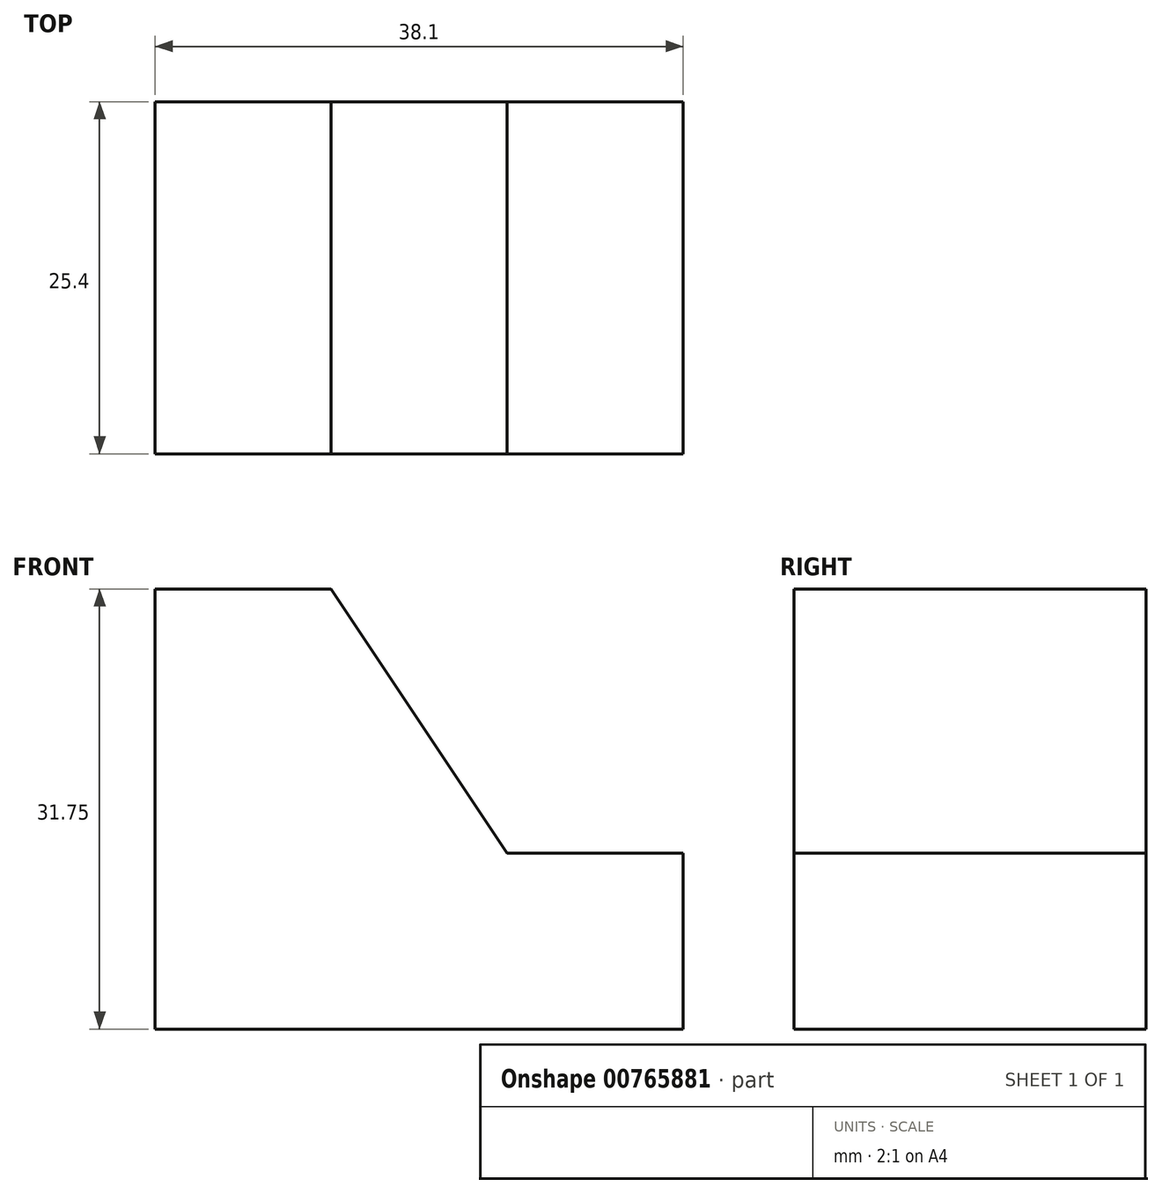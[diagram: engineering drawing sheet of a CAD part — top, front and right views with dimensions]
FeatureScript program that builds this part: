
annotation { "Feature Type Name" : "Feature", "Feature Type Description" : "" }
export const myFeature = defineFeature(function(context is Context, id is Id, definition is map)
    precondition{}
    {
        {
            var Q0;
            Q0=qCreatedBy(makeId("Front.planeOp"),FACE);
            var sketch = newSketch(context, id + "F0", { "sketchPlane" : qUnion([Q0])});
            skLineSegment(sketch, "E0", {"start": v(0, 0) * mm, "end": v(25.4, 0) * mm});
            skLineSegment(sketch, "E1", {"start": v(25.4, 0) * mm, "end": v(25.4, 12.7) * mm});
            skLineSegment(sketch, "E2", {"start": v(25.4, 12.7) * mm, "end": v(12.7, 12.7) * mm});
            skLineSegment(sketch, "E3", {"start": v(0, 0) * mm, "end": v(-12.7, 0) * mm});
            skLineSegment(sketch, "E4", {"start": v(-12.7, 0) * mm, "end": v(-12.7, 31.75) * mm});
            skLineSegment(sketch, "E5", {"start": v(-12.7, 31.75) * mm, "end": v(0, 31.75) * mm});
            skLineSegment(sketch, "E6", {"start": v(0, 31.75) * mm, "end": v(12.7, 12.7) * mm});
            skSolve(sketch);
        }
        {
            var Q0;
            Q0=makeQuery(id+"F0.imprint","IMPRINT",FACE,{"disambiguationData":[TD([[makeQuery(id+"F0.imprint","IMPRINT",EDGE,{"derivedFrom":sQuery(id+"F0.wireOp",EDGE,"E0")}),1.0]])]});
            extrude(context, id + "F1", {"entities" : qUnion([Q0]), "depth" : 25.4 * mm, "offsetDistance" : 25.4 * mm});
        }
    });
